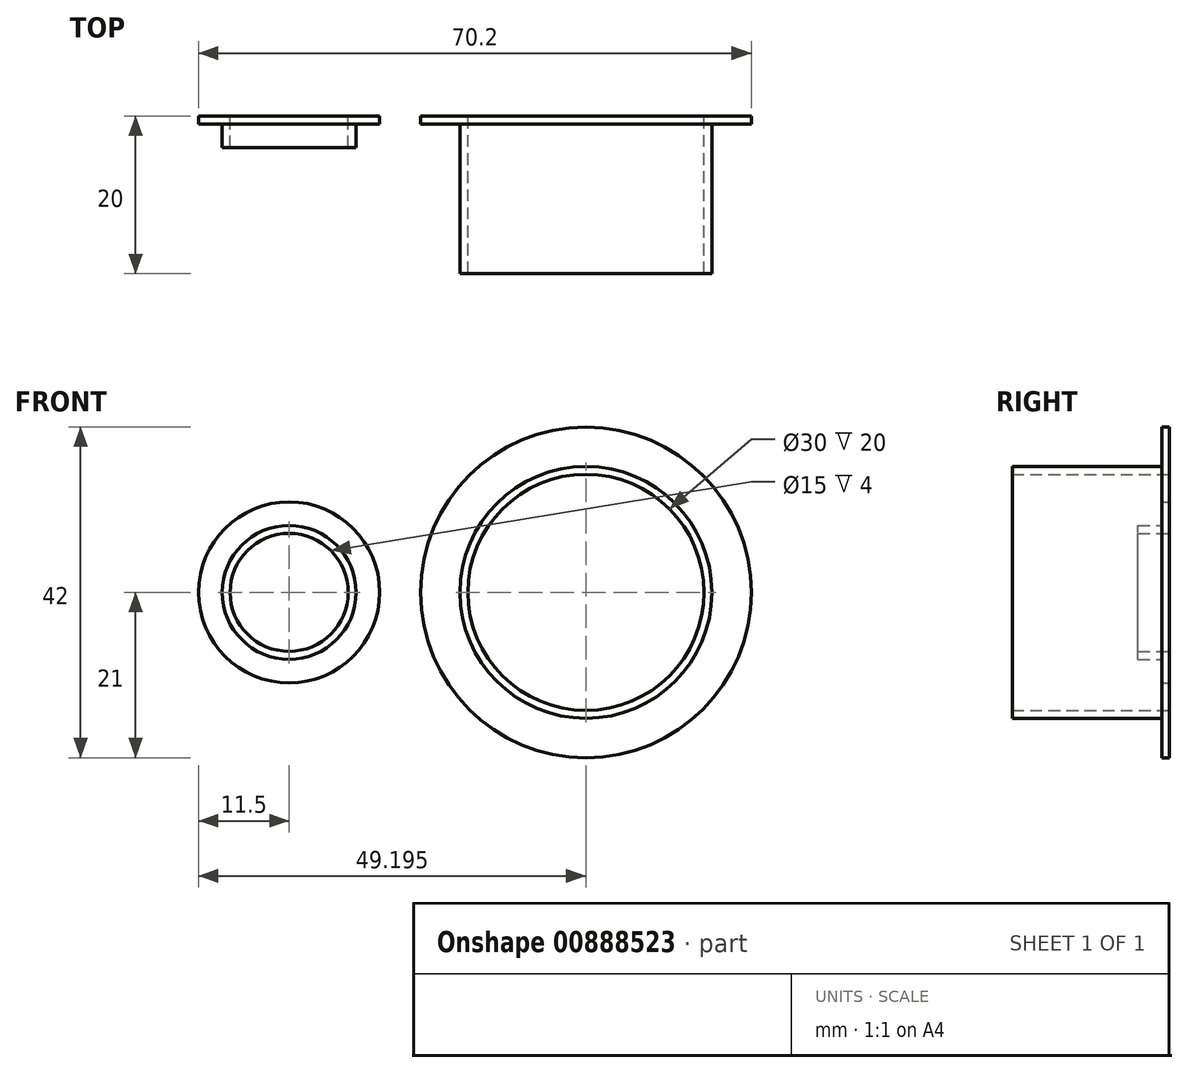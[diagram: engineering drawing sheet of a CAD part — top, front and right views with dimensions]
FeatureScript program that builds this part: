
annotation { "Feature Type Name" : "Feature", "Feature Type Description" : "" }
export const myFeature = defineFeature(function(context is Context, id is Id, definition is map)
    precondition{}
    {
        {
            var Q0;
            Q0=qCreatedBy(makeId("Front.planeOp"),FACE);
            var sketch = newSketch(context, id + "F0", { "sketchPlane" : qUnion([Q0])});
            skCircle(sketch, "E0", {"center": v(0, 0) * mm, "radius": 7.5 * mm});
            skCircle(sketch, "E1", {"center": v(0, 0) * mm, "radius": 8.5 * mm});
            skCircle(sketch, "E2.0", {"center": v(0, 0) * mm, "radius": 11.5 * mm});
            skSolve(sketch);
        }
        {
            var Q0;
            Q0=makeQuery(id+"F0.imprint","IMPRINT",FACE,{"disambiguationData":[TD([[makeQuery(id+"F0.imprint","IMPRINT",EDGE,{"derivedFrom":sQuery(id+"F0.wireOp",EDGE,"E0")}),-1.0]])]});
            extrude(context, id + "F1", {"entities" : qUnion([Q0]), "depth" : 4 * mm, "offsetDistance" : 25.4 * mm});
        }
        {
            var Q0;
            Q0=qCreatedBy(makeId("Front.planeOp"),FACE);
            var sketch = newSketch(context, id + "F2", { "sketchPlane" : qUnion([Q0])});
            skCircle(sketch, "E3", {"center": v(37.7, 0) * mm, "radius": 15 * mm});
            skCircle(sketch, "E4", {"center": v(37.7, 0) * mm, "radius": 16 * mm});
            skCircle(sketch, "E5.0", {"center": v(37.7, 0) * mm, "radius": 21 * mm});
            skSolve(sketch);
        }
        {
            var Q0;
            Q0=makeQuery(id+"F2.imprint","IMPRINT",FACE,{"disambiguationData":[TD([[makeQuery(id+"F2.imprint","IMPRINT",EDGE,{"derivedFrom":sQuery(id+"F2.wireOp",EDGE,"E3")}),-1.0]])]});
            var Q1;
            Q1=sQuery(id+"F2.wireOp",EDGE,"E3");
            var Q2;
            Q2=sQuery(id+"F2.wireOp",EDGE,"E4");
            extrude(context, id + "F3", {"entities" : qUnion([Q0]), "surfaceEntities" : qUnion([Q1, Q2]), "depth" : 20 * mm, "offsetDistance" : 25 * mm});
        }
        {
            var Q0;
            Q0=makeQuery(id+"F2.imprint","IMPRINT",FACE,{"disambiguationData":[TD([[makeQuery(id+"F2.imprint","IMPRINT",EDGE,{"derivedFrom":sQuery(id+"F2.wireOp",EDGE,"E4")}),-1.0]])]});
            extrude(context, id + "F4", {"entities" : qUnion([Q0]), "operationType" : NewBodyOperationType.ADD, "depth" : 1 * mm, "offsetDistance" : 25 * mm});
        }
        {
            var Q0;
            Q0=makeQuery(id+"F0.imprint","IMPRINT",FACE,{"disambiguationData":[TD([[makeQuery(id+"F0.imprint","IMPRINT",EDGE,{"derivedFrom":sQuery(id+"F0.wireOp",EDGE,"E1")}),-1.0]])]});
            extrude(context, id + "F5", {"entities" : qUnion([Q0]), "operationType" : NewBodyOperationType.ADD, "depth" : 1 * mm, "offsetDistance" : 25 * mm});
        }
    });
